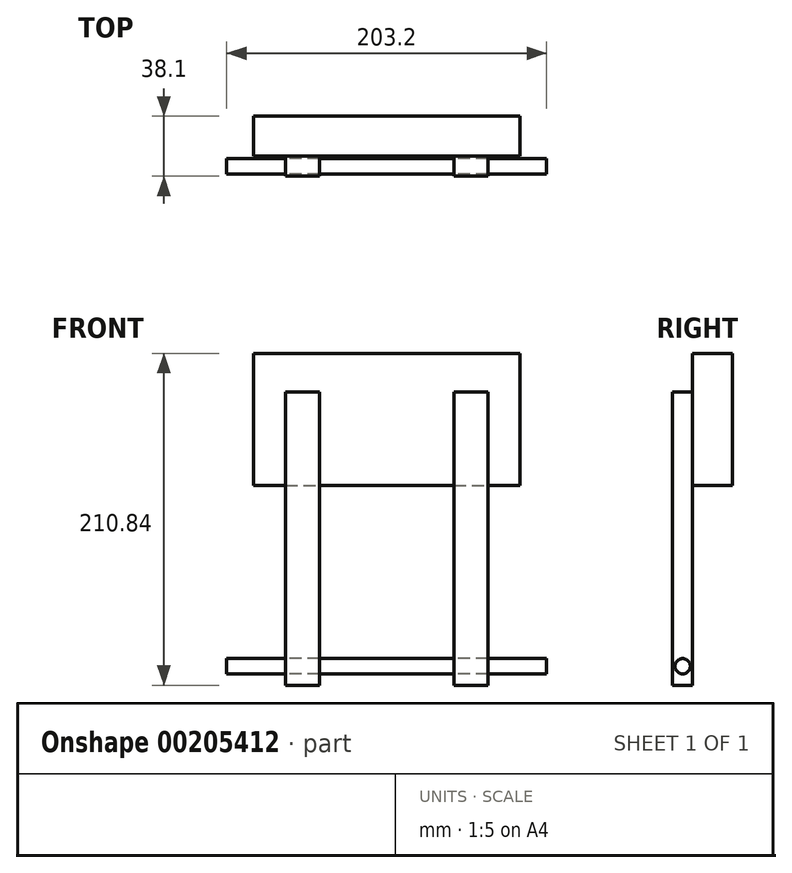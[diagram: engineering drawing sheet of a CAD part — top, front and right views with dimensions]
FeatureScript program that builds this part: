
annotation { "Feature Type Name" : "Feature", "Feature Type Description" : "" }
export const myFeature = defineFeature(function(context is Context, id is Id, definition is map)
    precondition{}
    {
        {
            var Q0;
            Q0=qCreatedBy(makeId("Front.planeOp"),FACE);
            var sketch = newSketch(context, id + "F0", { "sketchPlane" : qUnion([Q0])});
            skLineSegment(sketch, "E0.bottom", {"start": v(-84.62, 41.93) * mm, "end": v(84.62, 41.93) * mm});
            skLineSegment(sketch, "E0.top", {"start": v(-84.62, -41.93) * mm, "end": v(84.62, -41.93) * mm});
            skLineSegment(sketch, "E0.left", {"start": v(-84.62, 41.93) * mm, "end": v(-84.62, -41.93) * mm});
            skLineSegment(sketch, "E0.right", {"start": v(84.62, 41.93) * mm, "end": v(84.62, -41.93) * mm});
            skPoint(sketch, "E0.middle", {"position": v(0, 0) * mm});
            skLineSegment(sketch, "E1.bottom", {"start": v(-64.24, 17.35) * mm, "end": v(-42.75, 17.35) * mm});
            skLineSegment(sketch, "E1.top", {"start": v(-64.24, -168.9) * mm, "end": v(-42.75, -168.9) * mm});
            skLineSegment(sketch, "E1.left", {"start": v(-64.24, 17.35) * mm, "end": v(-64.24, -168.9) * mm});
            skLineSegment(sketch, "E1.right", {"start": v(-42.75, 17.35) * mm, "end": v(-42.75, -168.9) * mm});
            skLineSegment(sketch, "E2.MirrorCS", {"start": v(42.75, 17.35) * mm, "end": v(42.75, -168.9) * mm});
            skLineSegment(sketch, "E3.MirrorCS", {"start": v(64.24, -168.9) * mm, "end": v(42.75, -168.9) * mm});
            skLineSegment(sketch, "E4.MirrorCS", {"start": v(64.24, 17.35) * mm, "end": v(64.24, -168.9) * mm});
            skLineSegment(sketch, "E5.MirrorCS", {"start": v(64.24, 17.35) * mm, "end": v(42.75, 17.35) * mm});
            skSolve(sketch);
        }
        {
            var Q0;
            Q0=makeQuery(id+"F0.imprint","IMPRINT",FACE,{"disambiguationData":[TD([[makeQuery(id+"F0.imprint","IMPRINT",EDGE,{"derivedFrom":sQuery(id+"F0.wireOp",EDGE,"E0.bottom")}),-1.0]])]});
            var Q1;
            {var subQ5=sQuery(id+"F0.wireOp",EDGE,"E1.bottom");Q1=makeQuery(id+"F0.imprint","IMPRINT",FACE,{"disambiguationData":[TD([[makeQuery(id+"F0.imprint","IMPRINT",EDGE,{"derivedFrom":subQ5}),-1.0]])]});}
            var Q2;
            {var subQ5=sQuery(id+"F0.wireOp",EDGE,"E5.MirrorCS");Q2=makeQuery(id+"F0.imprint","IMPRINT",FACE,{"disambiguationData":[TD([[makeQuery(id+"F0.imprint","IMPRINT",EDGE,{"derivedFrom":subQ5}),1.0]])]});}
            extrude(context, id + "F1", {"entities" : qUnion([Q0, Q1, Q2]), "oppositeDirection" : true, "depth" : 25.4 * mm});
        }
        {
            var Q0;
            {var subQ5=sQuery(id+"F0.wireOp",EDGE,"E1.top");Q0=makeQuery(id+"F0.imprint","IMPRINT",FACE,{"disambiguationData":[TD([[makeQuery(id+"F0.imprint","IMPRINT",EDGE,{"derivedFrom":subQ5}),1.0]])]});}
            var Q1;
            {var subQ5=sQuery(id+"F0.wireOp",EDGE,"E1.bottom");Q1=makeQuery(id+"F0.imprint","IMPRINT",FACE,{"disambiguationData":[TD([[makeQuery(id+"F0.imprint","IMPRINT",EDGE,{"derivedFrom":subQ5}),-1.0]])]});}
            var Q2;
            {var subQ5=sQuery(id+"F0.wireOp",EDGE,"E3.MirrorCS");Q2=makeQuery(id+"F0.imprint","IMPRINT",FACE,{"disambiguationData":[TD([[makeQuery(id+"F0.imprint","IMPRINT",EDGE,{"derivedFrom":subQ5}),-1.0]])]});}
            var Q3;
            {var subQ5=sQuery(id+"F0.wireOp",EDGE,"E5.MirrorCS");Q3=makeQuery(id+"F0.imprint","IMPRINT",FACE,{"disambiguationData":[TD([[makeQuery(id+"F0.imprint","IMPRINT",EDGE,{"derivedFrom":subQ5}),1.0]])]});}
            extrude(context, id + "F2", {"entities" : qUnion([Q0, Q1, Q2, Q3]), "depth" : 12.7 * mm});
        }
        {
            var Q0;
            Q0=qCreatedBy(makeId("Right.planeOp"),FACE);
            var sketch = newSketch(context, id + "F3", { "sketchPlane" : qUnion([Q0])});
            skLineSegment(sketch, "E6.0", {"start": v(-12.7, -168.9) * mm, "end": v(0, -168.9) * mm, "construction": true});
            skCircle(sketch, "E7", {"center": v(-6.35, -156.81) * mm, "radius": 4.85 * mm});
            skPoint(sketch, "E7.centerSnap0", {"position": v(-6.35, -168.9) * mm});
            skSolve(sketch);
        }
        {
            var Q0;
            Q0 = qSketchRegion(id + "F3", true);
            extrude(context, id + "F4", {"entities" : qUnion([Q0]), "depth" : 203.2 * mm, "symmetric" : true});
        }
    });
